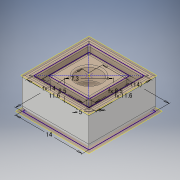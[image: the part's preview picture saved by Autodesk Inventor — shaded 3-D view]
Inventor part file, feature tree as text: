
AUTODESK INVENTOR PART (.ipt)
format: ipt  version: 2019.3 (Build 233278000, 278)  size: 256,512 bytes
history: native  units: in
note: dims shown in document units (in); Inventor stores cm internally (conversion verified against a paired STEP export)
features: fillet x7, extrude x4, sketch x2, other x1
ambient origin geometry x8: Origin, YZ Plane, XZ Plane, XY Plane, X Axis, Y Axis, Z Axis, Center Point
bodies: Body1 (feature_tree)
feature tree (14):
  other  "作業平面2"
  sketch  "スケッチ3"
  sketch  "スケッチ1"
  extrude  "押し出し8"  Depth=0.2559in
  extrude  "押し出し9"  Depth=0.3346in
  extrude  "押し出し10"  Depth=0.3346in
  extrude  "押し出し11"  Depth=0.4567in
  fillet  "フィレット2"  Radius=0.4567in
  fillet  "フィレット3"  Radius=0.2874in
  fillet  "フィレット4"  Radius=0.5512in
  fillet  "フィレット5"  Radius=0.5512in
  fillet  "フィレット6"  Radius=0.1969in
  fillet  "フィレット7"  Radius=0.2559in
  fillet  "フィレット8"  Radius=0.0787in
